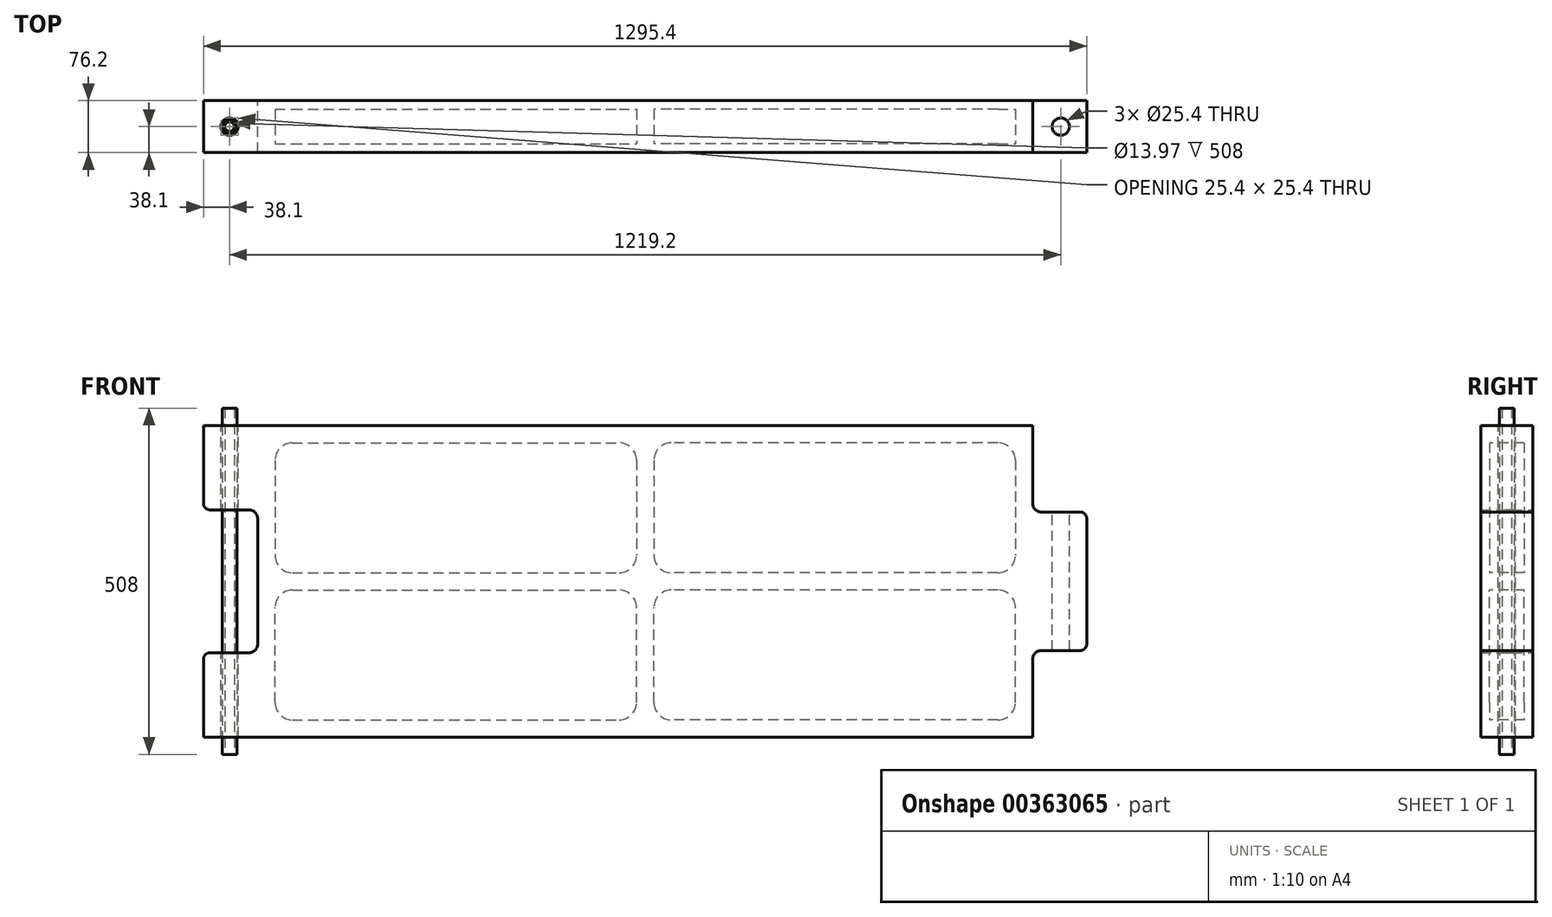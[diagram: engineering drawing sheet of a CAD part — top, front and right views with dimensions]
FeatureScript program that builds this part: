
annotation { "Feature Type Name" : "Feature", "Feature Type Description" : "" }
export const myFeature = defineFeature(function(context is Context, id is Id, definition is map)
    precondition{}
    {
        {
            var Q0;
            Q0=qCreatedBy(makeId("Front.planeOp"),FACE);
            var sketch = newSketch(context, id + "F0", { "sketchPlane" : qUnion([Q0])});
            skLineSegment(sketch, "E0.bottom", {"start": v(-568.33, 228.6) * mm, "end": v(568.32, 228.6) * mm});
            skLineSegment(sketch, "E0.top", {"start": v(-568.32, -228.6) * mm, "end": v(568.33, -228.6) * mm});
            skLineSegment(sketch, "E0.left", {"start": v(-568.33, 228.6) * mm, "end": v(-568.32, -228.6) * mm});
            skLineSegment(sketch, "E0.right", {"start": v(568.32, 228.6) * mm, "end": v(568.33, -228.6) * mm});
            skPoint(sketch, "E0.middle", {"position": v(0, 0) * mm});
            skLineSegment(sketch, "E1", {"start": v(-568.33, 228.6) * mm, "end": v(-647.7, 228.6) * mm});
            skLineSegment(sketch, "E2", {"start": v(-647.7, 228.6) * mm, "end": v(-647.7, 104.77) * mm});
            skLineSegment(sketch, "E3", {"start": v(-647.7, 104.77) * mm, "end": v(-568.32, 104.77) * mm});
            skLineSegment(sketch, "E4", {"start": v(-568.32, -228.6) * mm, "end": v(-647.7, -228.6) * mm});
            skLineSegment(sketch, "E5", {"start": v(-647.7, -228.6) * mm, "end": v(-647.7, -104.78) * mm});
            skLineSegment(sketch, "E6", {"start": v(-647.7, -104.78) * mm, "end": v(-568.32, -104.78) * mm});
            skLineSegment(sketch, "E7", {"start": v(568.32, 101.6) * mm, "end": v(647.7, 101.6) * mm});
            skLineSegment(sketch, "E8", {"start": v(647.7, 101.6) * mm, "end": v(647.7, -101.6) * mm});
            skLineSegment(sketch, "E9", {"start": v(647.7, -101.6) * mm, "end": v(568.32, -101.6) * mm});
            skPoint(sketch, "E10", {"position": v(647.7, 0) * mm});
            skSolve(sketch);
        }
        {
            var Q0;
            Q0 = qSketchRegion(id + "F0", true);
            extrude(context, id + "F1", {"entities" : qUnion([Q0]), "endBound" : BoundingType.SYMMETRIC, "depth" : 76.2 * mm, "hasSecondDirection" : true, "secondDirectionOppositeDirection" : true, "secondDirectionDepth" : 36.5 * mm, "offsetDistance" : 25.4 * mm});
        }
        {
            var Q0;
            Q0=qCreatedBy(makeId("Top.planeOp"),FACE);
            var sketch = newSketch(context, id + "F2", { "sketchPlane" : qUnion([Q0])});
            skCircle(sketch, "E11", {"center": v(-609.6, 0) * mm, "radius": 12.7 * mm});
            skCircle(sketch, "E12", {"center": v(609.6, 0) * mm, "radius": 12.7 * mm});
            skLineSegment(sketch, "E13", {"start": v(-609.6, 0) * mm, "end": v(609.6, 0) * mm, "construction": true});
            skPoint(sketch, "E14", {"position": v(0, 0) * mm});
            skSolve(sketch);
        }
        {
            var Q0;
            Q0 = qSketchRegion(id + "F2", true);
            extrude(context, id + "F3", {"entities" : qUnion([Q0]), "operationType" : NewBodyOperationType.REMOVE, "endBound" : BoundingType.SYMMETRIC, "oppositeDirection" : true, "depth" : 508 * mm});
        }
        {
            var Q0;
            Q0=makeQuery(id+"F1.opExtrude","SWEPT_EDGE",EDGE,{"disambiguationData":[OSD([sQuery(id+"F0.wireOp",EDGE,"E7"),sQuery(id+"F0.wireOp",EDGE,"E8")])]});
            var Q1;
            Q1=makeQuery(id+"F1.opExtrude","SWEPT_EDGE",EDGE,{"disambiguationData":[OSD([sQuery(id+"F0.wireOp",EDGE,"E8"),sQuery(id+"F0.wireOp",EDGE,"E9")])]});
            var Q2;
            Q2=makeQuery(id+"F1.opExtrude","SWEPT_EDGE",EDGE,{"disambiguationData":[OSD([sQuery(id+"F0.wireOp",EDGE,"E2"),sQuery(id+"F0.wireOp",EDGE,"E3")])]});
            var Q3;
            Q3=makeQuery(id+"F1.opExtrude","SWEPT_EDGE",EDGE,{"disambiguationData":[OSD([sQuery(id+"F0.wireOp",EDGE,"E5"),sQuery(id+"F0.wireOp",EDGE,"E6")])]});
            fillet(context, id + "F4", {"entities" : qUnion([Q0, Q1, Q2, Q3]), "radius" : 9.52 * mm, "tangentPropagation" : true, "allowEdgeOverflow" : false});
        }
        {
            var Q0;
            Q0=makeQuery(id+"F1.opExtrude","SWEPT_EDGE",EDGE,{"disambiguationData":[OSD([sQuery(id+"F0.wireOp",EDGE,"E0.left"),sQuery(id+"F0.wireOp",EDGE,"E3")])]});
            var Q1;
            Q1=makeQuery(id+"F1.opExtrude","SWEPT_EDGE",EDGE,{"disambiguationData":[OSD([sQuery(id+"F0.wireOp",EDGE,"E0.left"),sQuery(id+"F0.wireOp",EDGE,"E6")])]});
            var Q2;
            Q2=makeQuery(id+"F1.opExtrude","SWEPT_EDGE",EDGE,{"disambiguationData":[OSD([sQuery(id+"F0.wireOp",EDGE,"E0.right"),sQuery(id+"F0.wireOp",EDGE,"E9")])]});
            var Q3;
            Q3=makeQuery(id+"F1.opExtrude","SWEPT_EDGE",EDGE,{"disambiguationData":[OSD([sQuery(id+"F0.wireOp",EDGE,"E0.right"),sQuery(id+"F0.wireOp",EDGE,"E7")])]});
            fillet(context, id + "F5", {"entities" : qUnion([Q0, Q1, Q2, Q3]), "radius" : 12.7 * mm, "tangentPropagation" : true, "allowEdgeOverflow" : false});
        }
        {
            var Q0;
            Q0=qCreatedBy(makeId("Front.planeOp"),FACE);
            var sketch = newSketch(context, id + "F6", { "sketchPlane" : qUnion([Q0])});
            skPoint(sketch, "E15.middle", {"position": v(0, 0) * mm});
            skLineSegment(sketch, "E16.bottom", {"start": v(-517.52, 203.2) * mm, "end": v(-38.1, 203.2) * mm});
            skLineSegment(sketch, "E16.top", {"start": v(-517.52, 12.7) * mm, "end": v(-38.1, 12.7) * mm});
            skLineSegment(sketch, "E16.left", {"start": v(-542.92, 177.8) * mm, "end": v(-542.92, 38.1) * mm});
            skLineSegment(sketch, "E16.right", {"start": v(-12.7, 177.8) * mm, "end": v(-12.7, 38.1) * mm});
            skLineSegment(sketch, "E17", {"start": v(0, 0) * mm, "end": v(0, 71.22) * mm, "construction": true});
            skLineSegment(sketch, "E18", {"start": v(0, 0) * mm, "end": v(-136.97, 0) * mm, "construction": true});
            skPoint(sketch, "E19.visualSharp", {"position": v(-12.7, 12.7) * mm});
            skArc(sketch, "E19.filletArc", {"start": v(-38.1, 12.7) * mm, "mid": v(-20.14, 20.14) * mm, "end": v(-12.7, 38.1) * mm});
            skPoint(sketch, "E20.visualSharp", {"position": v(-12.7, 203.2) * mm});
            skArc(sketch, "E20.filletArc", {"start": v(-12.7, 177.8) * mm, "mid": v(-20.14, 195.76) * mm, "end": v(-38.1, 203.2) * mm});
            skPoint(sketch, "E21.visualSharp", {"position": v(-542.92, 203.2) * mm});
            skArc(sketch, "E21.filletArc", {"start": v(-517.52, 203.2) * mm, "mid": v(-535.49, 195.76) * mm, "end": v(-542.92, 177.8) * mm});
            skPoint(sketch, "E22.visualSharp", {"position": v(-542.92, 12.7) * mm});
            skArc(sketch, "E22.filletArc", {"start": v(-542.92, 38.1) * mm, "mid": v(-535.49, 20.14) * mm, "end": v(-517.52, 12.7) * mm});
            skLineSegment(sketch, "E23.MirrorCS", {"start": v(12.7, 177.8) * mm, "end": v(12.7, 38.1) * mm});
            skPoint(sketch, "E24.MirrorP", {"position": v(12.7, 203.2) * mm});
            skArc(sketch, "E25.MirrorCS", {"start": v(12.7, 177.8) * mm, "mid": v(20.14, 195.76) * mm, "end": v(38.1, 203.2) * mm});
            skLineSegment(sketch, "E26.MirrorCS", {"start": v(517.52, 203.2) * mm, "end": v(38.1, 203.2) * mm});
            skPoint(sketch, "E27.MirrorP", {"position": v(542.92, 203.2) * mm});
            skArc(sketch, "E28.MirrorCS", {"start": v(517.52, 203.2) * mm, "mid": v(535.49, 195.76) * mm, "end": v(542.92, 177.8) * mm});
            skLineSegment(sketch, "E29.MirrorCS", {"start": v(542.92, 177.8) * mm, "end": v(542.92, 38.1) * mm});
            skArc(sketch, "E30.MirrorCS", {"start": v(542.92, 38.1) * mm, "mid": v(535.49, 20.14) * mm, "end": v(517.52, 12.7) * mm});
            skPoint(sketch, "E31.MirrorP", {"position": v(542.92, 12.7) * mm});
            skLineSegment(sketch, "E32.MirrorCS", {"start": v(517.52, 12.7) * mm, "end": v(38.1, 12.7) * mm});
            skPoint(sketch, "E33.MirrorP", {"position": v(12.7, 12.7) * mm});
            skArc(sketch, "E34.MirrorCS", {"start": v(38.1, 12.7) * mm, "mid": v(20.14, 20.14) * mm, "end": v(12.7, 38.1) * mm});
            skArc(sketch, "E35.MirrorCS", {"start": v(38.1, -12.7) * mm, "mid": v(20.14, -20.14) * mm, "end": v(12.7, -38.1) * mm});
            skArc(sketch, "E36.MirrorCS", {"start": v(542.92, -38.1) * mm, "mid": v(535.49, -20.14) * mm, "end": v(517.52, -12.7) * mm});
            skArc(sketch, "E37.MirrorCS", {"start": v(-517.52, -203.2) * mm, "mid": v(-535.49, -195.76) * mm, "end": v(-542.92, -177.8) * mm});
            skArc(sketch, "E38.MirrorCS", {"start": v(-38.1, -12.7) * mm, "mid": v(-20.14, -20.14) * mm, "end": v(-12.7, -38.1) * mm});
            skPoint(sketch, "E39.MirrorP", {"position": v(12.7, -12.7) * mm});
            skArc(sketch, "E40.MirrorCS", {"start": v(-542.92, -38.1) * mm, "mid": v(-535.49, -20.14) * mm, "end": v(-517.52, -12.7) * mm});
            skArc(sketch, "E41.MirrorCS", {"start": v(517.52, -203.2) * mm, "mid": v(535.49, -195.76) * mm, "end": v(542.92, -177.8) * mm});
            skArc(sketch, "E42.MirrorCS", {"start": v(-12.7, -177.8) * mm, "mid": v(-20.14, -195.76) * mm, "end": v(-38.1, -203.2) * mm});
            skArc(sketch, "E43.MirrorCS", {"start": v(12.7, -177.8) * mm, "mid": v(20.14, -195.76) * mm, "end": v(38.1, -203.2) * mm});
            skLineSegment(sketch, "E44.MirrorCS", {"start": v(0, 0) * mm, "end": v(0, -71.22) * mm, "construction": true});
            skPoint(sketch, "E45.MirrorP", {"position": v(542.92, -12.7) * mm});
            skPoint(sketch, "E46.MirrorP", {"position": v(-12.7, -12.7) * mm});
            skLineSegment(sketch, "E47.MirrorCS", {"start": v(-517.52, -203.2) * mm, "end": v(-38.1, -203.2) * mm});
            skPoint(sketch, "E48.MirrorP", {"position": v(12.7, -203.2) * mm});
            skPoint(sketch, "E49.MirrorP", {"position": v(-542.92, -12.7) * mm});
            skPoint(sketch, "E50.MirrorP", {"position": v(-542.92, -203.2) * mm});
            skLineSegment(sketch, "E51.MirrorCS", {"start": v(542.92, -177.8) * mm, "end": v(542.92, -38.1) * mm});
            skPoint(sketch, "E52.MirrorP", {"position": v(542.92, -203.2) * mm});
            skLineSegment(sketch, "E53.MirrorCS", {"start": v(12.7, -177.8) * mm, "end": v(12.7, -38.1) * mm});
            skLineSegment(sketch, "E54.MirrorCS", {"start": v(-542.92, -177.8) * mm, "end": v(-542.92, -38.1) * mm});
            skLineSegment(sketch, "E55.MirrorCS", {"start": v(517.52, -203.2) * mm, "end": v(38.1, -203.2) * mm});
            skLineSegment(sketch, "E56.MirrorCS", {"start": v(517.52, -12.7) * mm, "end": v(38.1, -12.7) * mm});
            skPoint(sketch, "E57.MirrorP", {"position": v(-12.7, -203.2) * mm});
            skLineSegment(sketch, "E58.MirrorCS", {"start": v(-517.52, -12.7) * mm, "end": v(-38.1, -12.7) * mm});
            skLineSegment(sketch, "E59.MirrorCS", {"start": v(-12.7, -177.8) * mm, "end": v(-12.7, -38.1) * mm});
            skSolve(sketch);
        }
        {
            var Q0;
            Q0 = qSketchRegion(id + "F6", true);
            extrude(context, id + "F7", {"entities" : qUnion([Q0]), "operationType" : NewBodyOperationType.REMOVE, "endBound" : BoundingType.SYMMETRIC, "oppositeDirection" : true, "depth" : 50.8 * mm, "offsetDistance" : 25.4 * mm});
        }
        {
            var Q0;
            Q0=qCreatedBy(makeId("Top.planeOp"),FACE);
            var sketch = newSketch(context, id + "F8", { "sketchPlane" : qUnion([Q0])});
            skCircle(sketch, "E60", {"center": v(-609.6, 0) * mm, "radius": 10.67 * mm});
            skCircle(sketch, "E61.0", {"center": v(-609.6, 0) * mm, "radius": 12.7 * mm});
            skCircle(sketch, "E62", {"center": v(-609.6, 0) * mm, "radius": 6.99 * mm});
            skSolve(sketch);
        }
        {
            var Q0;
            Q0=makeQuery(id+"F8.imprint","IMPRINT",FACE,{"disambiguationData":[TD([[makeQuery(id+"F8.imprint","IMPRINT",EDGE,{"derivedFrom":sQuery(id+"F8.wireOp",EDGE,"E60")}),1.0]])]});
            extrude(context, id + "F9", {"entities" : qUnion([Q0]), "endBound" : BoundingType.SYMMETRIC, "depth" : 508 * mm});
        }
    });
